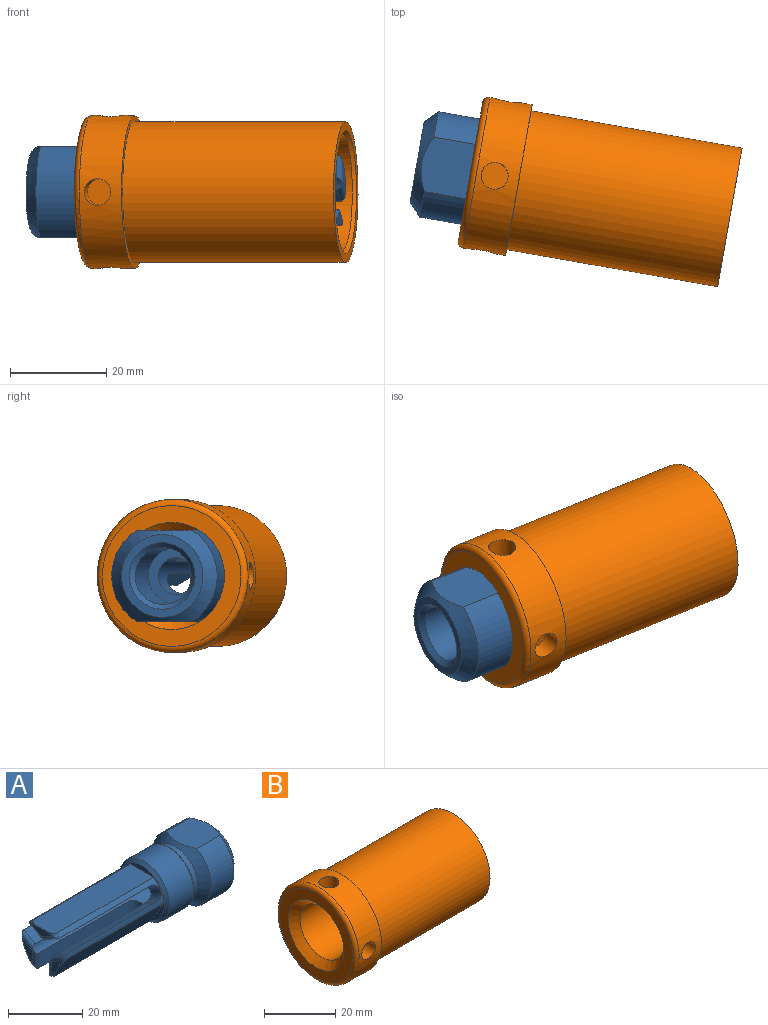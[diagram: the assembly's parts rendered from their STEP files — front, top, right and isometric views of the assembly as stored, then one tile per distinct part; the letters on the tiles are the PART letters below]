
ASSEMBLY  parts=2 mates=1
PART A: 49 faces, bbox 64.6x22.2x22.2 mm
  f0: plane 5.77x3.33mm, normal (-1,0,0), area 10.2mm2, adj f7,f13,f45,f46
  f1: cylinder r=3.81mm len=47.82mm, axis (1,0,0), area 563.6mm2, adj f23,f34,f35,f36,f37,f38,f39,f40
  f2: torus R=6.99mm, axis (-1,0,0), area 3.6mm2, adj f4,f14,f31,f44
  f3: cylinder r=8.26mm len=36.83mm, axis (1,0,0), area 59.8mm2, adj f13,f21,f32,f38,f40
  f4: plane 5.77x3.33mm, normal (-1,0,0), area 10.2mm2, adj f2,f11,f43,f44
  f5: torus R=6.99mm, axis (-1,0,0), area 3.6mm2, adj f9,f22,f33,f48
  f6: cylinder r=8.26mm len=36.83mm, axis (1,0,0), area 59.8mm2, adj f11,f21,f31,f36,f41
  f7: torus R=6.99mm, axis (-1,0,0), area 3.6mm2, adj f0,f12,f32,f45
  f8: cylinder r=8.26mm len=36.83mm, axis (1,0,0), area 59.8mm2, adj f10,f21,f33,f34,f42
  f9: plane 6.66x2.77mm, normal (-1,0,0), area 10.2mm2, adj f5,f10,f47,f48
  f10: torus R=6.99mm, axis (-1,0,0), area 3.6mm2, adj f8,f9,f33,f47
  f11: torus R=6.99mm, axis (-1,0,0), area 3.6mm2, adj f4,f6,f31,f43
  f12: cylinder r=8.26mm len=36.83mm, axis (1,0,0), area 59.8mm2, adj f7,f21,f32,f35,f42
  f13: torus R=6.99mm, axis (-1,0,0), area 3.6mm2, adj f0,f3,f32,f46
  f14: cylinder r=8.26mm len=36.83mm, axis (1,0,0), area 59.8mm2, adj f2,f21,f31,f39,f40
  f15: cylinder r=11.11mm len=19.05mm, axis (1,0,0), area 199.5mm2, adj f17,f18,f27,f28
  f16: cylinder r=11.11mm len=19.05mm, axis (1,0,0), area 199.5mm2, adj f17,f18,f27,f28
  f17: cone r=8.57mm half-angle=45deg, axis (1,0,0), area 187.4mm2, adj f15,f16,f19,f27,f28
  f18: cone r=8.57mm half-angle=45deg, axis (-1,0,0), area 187.4mm2, adj f15,f16,f26,f27,f28
  f19: cylinder r=8.57mm len=17.15mm, axis (1,0,0), area 85.5mm2, adj f17,f30
  f20: cylinder r=9.53mm len=19.05mm, axis (1,0,0), area 550.3mm2, adj f29,f30
  f21: plane 17.12x17.12mm, normal (-1,0,0), area 38.8mm2, adj f3,f6,f8,f12,f14,f22,f29,f31
  f22: cylinder r=8.26mm len=36.83mm, axis (1,0,0), area 59.8mm2, adj f5,f21,f33,f37,f41
  f23: plane 11.79x11.79mm, normal (1,0,0), area 63.5mm2, adj f1,f24
  f24: cylinder r=5.89mm len=15.71mm, axis (1,0,0), area 581.6mm2, adj f23,f25
  f25: cone r=5.89mm half-angle=45deg, axis (1,0,0), area 57.8mm2, adj f24,f26
  f26: plane 17.15x17.15mm, normal (1,0,0), area 80.9mm2, adj f18,f25
  f27: plane 11.91x11.46mm, normal (0,0,1), area 123.6mm2, adj f15,f16,f17,f18
  f28: plane 11.91x11.46mm, normal (0,0,-1), area 123.6mm2, adj f15,f16,f17,f18
  f29: cone r=9.53mm half-angle=45deg, axis (1,0,0), area 77.6mm2, adj f20,f21
  f30: cone r=8.56mm half-angle=45deg, axis (-1,0,0), area 76.6mm2, adj f19,f20
  f31: plane 38.1x7.62mm, normal (0,-0.87,-0.5), area 333.8mm2, adj f2,f6,f11,f14,f21
  f32: plane 38.1x7.62mm, normal (0,0.87,-0.5), area 333.8mm2, adj f3,f7,f12,f13,f21
  f33: plane 38.1x8.8mm, normal (0,0,1), area 333.8mm2, adj f5,f8,f10,f21,f22
  f34: plane 34.45x4.27mm, normal (0,0.5,-0.87), area 169.8mm2, adj f1,f8,f42,f47
  f35: plane 34.45x4.27mm, normal (0,-0.5,0.87), area 169.8mm2, adj f1,f12,f42,f45
  f36: plane 34.45x4.27mm, normal (0,0.5,0.87), area 169.8mm2, adj f1,f6,f41,f43
  f37: plane 34.45x4.27mm, normal (0,-0.5,-0.87), area 169.8mm2, adj f1,f22,f41,f48
  f38: plane 34.45x4.93mm, normal (0,-1,0), area 169.8mm2, adj f1,f3,f40,f46
  f39: plane 34.45x4.93mm, normal (0,1,0), area 169.8mm2, adj f1,f14,f40,f44
  f40: cylinder r=2.38mm len=5.28mm, axis (0,0,-1), area 35.1mm2, adj f1,f3,f14,f38,f39
  f41: cylinder r=2.38mm len=6.95mm, axis (0,-0.87,0.5), area 35.1mm2, adj f1,f6,f22,f36,f37
  f42: cylinder r=2.38mm len=6.95mm, axis (0,-0.87,-0.5), area 35.1mm2, adj f1,f8,f12,f34,f35
  f43: cylinder r=1.27mm len=5.83mm, axis (0,0.87,-0.5), area 9.4mm2, adj f1,f4,f11,f36,f44
  f44: cylinder r=1.27mm len=6mm, axis (0,0,-1), area 9.4mm2, adj f1,f2,f4,f39,f43
  f45: cylinder r=1.27mm len=5.83mm, axis (0,0.87,0.5), area 9.4mm2, adj f0,f1,f7,f35,f46
  f46: cylinder r=1.27mm len=6mm, axis (0,0,1), area 9.4mm2, adj f0,f1,f13,f38,f45
  f47: cylinder r=1.27mm len=5.83mm, axis (0,-0.87,-0.5), area 9.4mm2, adj f1,f9,f10,f34,f48
  f48: cylinder r=1.27mm len=5.83mm, axis (0,-0.87,0.5), area 9.4mm2, adj f1,f5,f9,f37,f47
PART B: 19 faces, bbox 54.6x34.4x34.4 mm
  f0: cylinder r=2.8mm len=5.59mm, axis (0,-1,0), area 70.3mm2, adj f1,f10
  f1: plane 5.59x5.59mm, normal (0,-1,0), area 24.6mm2, adj f0
  f2: cylinder r=2.8mm len=5.59mm, axis (0,0,-1), area 70.3mm2, adj f3,f10
  f3: plane 5.59x5.59mm, normal (0,0,-1), area 24.6mm2, adj f2
  f4: cylinder r=2.8mm len=5.59mm, axis (0,1,0), area 70.3mm2, adj f5,f10
  f5: plane 5.59x5.59mm, normal (0,1,0), area 24.6mm2, adj f4
  f6: cylinder r=12.06mm len=38.61mm, axis (-1,0,0), area 2926.7mm2, adj f14,f15
  f7: plane 29.21x29.21mm, normal (1,0,0), area 153.2mm2, adj f8,f15
  f8: cylinder r=14.61mm len=44.45mm, axis (-1,0,0), area 4079mm2, adj f7,f9
  f9: plane 31.75x31.75mm, normal (1,0,0), area 121.6mm2, adj f8,f10
  f10: cylinder r=15.88mm len=31.75mm, axis (-1,0,0), area 788.6mm2, adj f0,f2,f4,f9,f16,f18
  f11: plane 29.21x29.21mm, normal (-1,0,0), area 282.2mm2, adj f12,f18
  f12: cone r=11.11mm half-angle=45deg, axis (-1,0,0), area 208.5mm2, adj f11,f13
  f13: cylinder r=8.75mm len=17.5mm, axis (-1,0,0), area 708mm2, adj f12,f14
  f14: plane 24.13x24.13mm, normal (1,0,0), area 216.8mm2, adj f6,f13
  f15: cone r=12.83mm half-angle=45deg, axis (1,0,0), area 84.3mm2, adj f6,f7
  f16: cylinder r=2.8mm len=5.59mm, axis (0,0,1), area 70.3mm2, adj f10,f17
  f17: plane 5.59x5.59mm, normal (0,0,1), area 24.6mm2, adj f16
  f18: torus R=14.61mm, axis (1,0,0), area 193.2mm2, adj f10,f11
PLACE A rot(axis=(0.09,1,0),180deg) t=(67.3,24.34,34.55)mm
PLACE B rot(axis=(0,0,-1),10deg) t=(132.58,12.83,34.55)mm
MATE planar A.f1 <-> B.f6  axis (-0.98,0.17,0) through (78.8,22.32,34.55)mm
